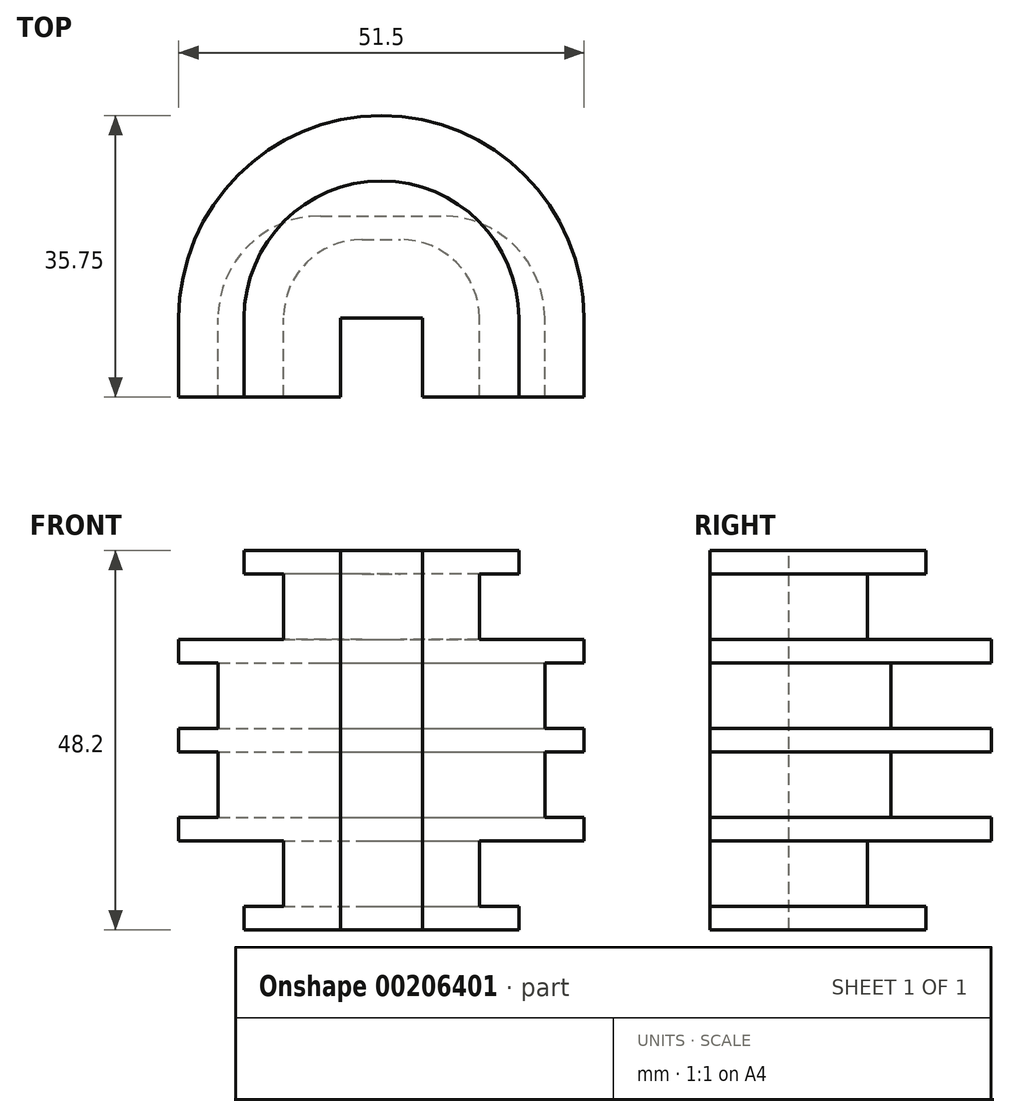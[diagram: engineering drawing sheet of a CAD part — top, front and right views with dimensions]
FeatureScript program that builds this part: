
annotation { "Feature Type Name" : "Feature", "Feature Type Description" : "" }
export const myFeature = defineFeature(function(context is Context, id is Id, definition is map)
    precondition{}
    {
        {
            assignVariable(context, id + "F0", {"name" : "slot", "anyValue" : 8.3});
        }
        {
            var Q0;
            Q0=qCreatedBy(makeId("Top.planeOp"),FACE);
            var sketch = newSketch(context, id + "F1", { "sketchPlane" : qUnion([Q0])});
            skLineSegment(sketch, "E0", {"start": v(-12.45, 0) * mm, "end": v(12.45, 0) * mm});
            skLineSegment(sketch, "E1", {"start": v(0, 10) * mm, "end": v(2.45, 10) * mm});
            skArc(sketch, "E2", {"start": v(2.45, 10) * mm, "mid": v(9.52, 7.07) * mm, "end": v(12.45, 0) * mm});
            skLineSegment(sketch, "E3.MirrorCS", {"start": v(0, 10) * mm, "end": v(-2.45, 10) * mm});
            skArc(sketch, "E4.MirrorCS", {"start": v(-2.45, 10) * mm, "mid": v(-9.52, 7.07) * mm, "end": v(-12.45, 0) * mm});
            skSolve(sketch);
        }
        {
            var Q0;
            Q0 = qSketchRegion(id + "F1", true);
            extrude(context, id + "F2", {"entities" : qUnion([Q0]), "depth" : (getVariable(context, 'slot')) * mm});
        }
        {
            var Q0;
            Q0=makeQuery(id+"F2.opExtrude","CAP_FACE",FACE,{"disambiguationData":[OSD([sQuery(id+"F1.wireOp",EDGE,"E0"),sQuery(id+"F1.wireOp",EDGE,"l2TL0GOp-FfTA-6rHu-1I54-9TwRSkG5pjle")])],"isStart":false});
            var sketch = newSketch(context, id + "F3", { "sketchPlane" : qUnion([Q0])});
            skArc(sketch, "E5", {"start": v(-17.45, 0) * mm, "mid": v(0, 17.45) * mm, "end": v(17.45, 0) * mm});
            skLineSegment(sketch, "E6", {"start": v(-17.45, 0) * mm, "end": v(17.45, 0) * mm});
            skSolve(sketch);
        }
        {
            var Q0;
            Q0 = qSketchRegion(id + "F3", true);
            extrude(context, id + "F4", {"entities" : qUnion([Q0]), "operationType" : NewBodyOperationType.ADD, "depth" : 3 * mm});
        }
        {
            var Q0;
            Q0=makeQuery(id+"F2.opExtrude","CAP_FACE",FACE,{"disambiguationData":[OSD([sQuery(id+"F1.wireOp",EDGE,"E0"),sQuery(id+"F1.wireOp",EDGE,"l2TL0GOp-FfTA-6rHu-1I54-9TwRSkG5pjle")])],"isStart":true});
            var sketch = newSketch(context, id + "F5", { "sketchPlane" : qUnion([Q0])});
            skArc(sketch, "E7", {"start": v(25.75, 0) * mm, "mid": v(0, -25.75) * mm, "end": v(-25.75, 0) * mm});
            skLineSegment(sketch, "E8", {"start": v(25.75, 0) * mm, "end": v(-25.75, 0) * mm});
            skSolve(sketch);
        }
        {
            var Q0;
            Q0 = qSketchRegion(id + "F5", true);
            extrude(context, id + "F6", {"entities" : qUnion([Q0]), "operationType" : NewBodyOperationType.ADD, "depth" : 3 * mm});
        }
        {
            var Q0;
            Q0=makeQuery(id+"F6.opExtrude","CAP_FACE",FACE,{"disambiguationData":[OSD([sQuery(id+"F5.wireOp",EDGE,"E7"),sQuery(id+"F5.wireOp",EDGE,"E8")])],"isStart":false});
            var sketch = newSketch(context, id + "F7", { "sketchPlane" : qUnion([Q0])});
            skLineSegment(sketch, "E9", {"start": v(20.75, 0) * mm, "end": v(-20.75, 0) * mm});
            skLineSegment(sketch, "E10", {"start": v(-7.75, -13) * mm, "end": v(0, -13) * mm});
            skArc(sketch, "E11", {"start": v(-7.75, -13) * mm, "mid": v(-16.94, -9.2) * mm, "end": v(-20.75, 0) * mm});
            skLineSegment(sketch, "E12.MirrorCS", {"start": v(7.75, -13) * mm, "end": v(0, -13) * mm});
            skArc(sketch, "E13.MirrorCS", {"start": v(7.75, -13) * mm, "mid": v(16.94, -9.2) * mm, "end": v(20.75, 0) * mm});
            skSolve(sketch);
        }
        {
            var Q0;
            Q0 = qSketchRegion(id + "F7", true);
            extrude(context, id + "F8", {"entities" : qUnion([Q0]), "operationType" : NewBodyOperationType.ADD, "depth" : (getVariable(context, 'slot')) * mm});
        }
        {
            var Q0;
            Q0=makeQuery(id+"F8.opExtrude","CAP_FACE",FACE,{"disambiguationData":[OSD([sQuery(id+"F7.wireOp",EDGE,"E9"),sQuery(id+"F7.wireOp",EDGE,"E10"),sQuery(id+"F7.wireOp",EDGE,"E11"),sQuery(id+"F7.wireOp",EDGE,"E12.MirrorCS"),sQuery(id+"F7.wireOp",EDGE,"E13.MirrorCS")])],"isStart":false});
            var sketch = newSketch(context, id + "F9", { "sketchPlane" : qUnion([Q0])});
            skArc(sketch, "E14", {"start": v(25.75, 0) * mm, "mid": v(0, -25.75) * mm, "end": v(-25.75, 0) * mm});
            skPoint(sketch, "E14.startSnap0", {"position": v(0, 0) * mm});
            skLineSegment(sketch, "E15", {"start": v(25.75, 0) * mm, "end": v(-25.75, 0) * mm});
            skSolve(sketch);
        }
        {
            var Q0;
            Q0 = qSketchRegion(id + "F9", true);
            extrude(context, id + "F10", {"entities" : qUnion([Q0]), "operationType" : NewBodyOperationType.ADD, "depth" : 3 * mm});
        }
        {
            var Q0;
            Q0=makeQuery(id+"F10.opExtrude","CAP_FACE",FACE,{"disambiguationData":[OSD([sQuery(id+"F9.wireOp",EDGE,"E14"),sQuery(id+"F9.wireOp",EDGE,"E15")])],"isStart":false});
            var sketch = newSketch(context, id + "F11", { "sketchPlane" : qUnion([Q0])});
            skLineSegment(sketch, "E16", {"start": v(20.75, 0) * mm, "end": v(-20.75, 0) * mm});
            skLineSegment(sketch, "E17", {"start": v(-7.75, -13) * mm, "end": v(0, -13) * mm});
            skArc(sketch, "E18", {"start": v(-7.75, -13) * mm, "mid": v(-16.94, -9.2) * mm, "end": v(-20.75, 0) * mm});
            skLineSegment(sketch, "E19.MirrorCS", {"start": v(7.75, -13) * mm, "end": v(0, -13) * mm});
            skArc(sketch, "E20.MirrorCS", {"start": v(7.75, -13) * mm, "mid": v(16.94, -9.2) * mm, "end": v(20.75, 0) * mm});
            skSolve(sketch);
        }
        {
            var Q0;
            Q0 = qSketchRegion(id + "F11", true);
            extrude(context, id + "F12", {"entities" : qUnion([Q0]), "operationType" : NewBodyOperationType.ADD, "depth" : (getVariable(context, 'slot')) * mm});
        }
        {
            var Q0;
            Q0=makeQuery(id+"F12.opExtrude","CAP_FACE",FACE,{"disambiguationData":[OSD([sQuery(id+"F11.wireOp",EDGE,"E16"),sQuery(id+"F11.wireOp",EDGE,"E17"),sQuery(id+"F11.wireOp",EDGE,"E18"),sQuery(id+"F11.wireOp",EDGE,"E19.MirrorCS"),sQuery(id+"F11.wireOp",EDGE,"E20.MirrorCS")])],"isStart":false});
            var sketch = newSketch(context, id + "F13", { "sketchPlane" : qUnion([Q0])});
            skArc(sketch, "E21", {"start": v(25.75, 0) * mm, "mid": v(0, -25.75) * mm, "end": v(-25.75, 0) * mm});
            skPoint(sketch, "E21.startSnap0", {"position": v(0, 0) * mm});
            skLineSegment(sketch, "E22", {"start": v(25.75, 0) * mm, "end": v(-25.75, 0) * mm});
            skSolve(sketch);
        }
        {
            var Q0;
            Q0 = qSketchRegion(id + "F13", true);
            extrude(context, id + "F14", {"entities" : qUnion([Q0]), "operationType" : NewBodyOperationType.ADD, "depth" : 3 * mm});
        }
        {
            var Q0;
            Q0=makeQuery(id+"F14.opExtrude","CAP_FACE",FACE,{"disambiguationData":[OSD([sQuery(id+"F13.wireOp",EDGE,"E21"),sQuery(id+"F13.wireOp",EDGE,"E22")])],"isStart":false});
            var sketch = newSketch(context, id + "F15", { "sketchPlane" : qUnion([Q0])});
            skLineSegment(sketch, "E23", {"start": v(0, -10) * mm, "end": v(2.45, -10) * mm});
            skArc(sketch, "E24", {"start": v(2.45, -10) * mm, "mid": v(9.52, -7.07) * mm, "end": v(12.45, 0) * mm});
            skLineSegment(sketch, "E25", {"start": v(12.45, 0) * mm, "end": v(0, 0) * mm});
            skLineSegment(sketch, "E26.MirrorCS", {"start": v(0, -10) * mm, "end": v(-2.45, -10) * mm});
            skArc(sketch, "E27.MirrorCS", {"start": v(-2.45, -10) * mm, "mid": v(-9.52, -7.07) * mm, "end": v(-12.45, 0) * mm});
            skLineSegment(sketch, "E28.MirrorCS", {"start": v(-12.45, 0) * mm, "end": v(0, 0) * mm});
            skSolve(sketch);
        }
        {
            var Q0;
            Q0 = qSketchRegion(id + "F15", true);
            extrude(context, id + "F16", {"entities" : qUnion([Q0]), "operationType" : NewBodyOperationType.ADD, "depth" : (getVariable(context, 'slot')) * mm});
        }
        {
            var Q0;
            Q0=makeQuery(id+"F16.opExtrude","CAP_FACE",FACE,{"disambiguationData":[OSD([sQuery(id+"F15.wireOp",EDGE,"E23"),sQuery(id+"F15.wireOp",EDGE,"E24"),sQuery(id+"F15.wireOp",EDGE,"E25"),sQuery(id+"F15.wireOp",EDGE,"E26.MirrorCS"),sQuery(id+"F15.wireOp",EDGE,"E27.MirrorCS"),sQuery(id+"F15.wireOp",EDGE,"E28.MirrorCS")])],"isStart":false});
            var sketch = newSketch(context, id + "F17", { "sketchPlane" : qUnion([Q0])});
            skArc(sketch, "E29", {"start": v(17.45, 0) * mm, "mid": v(0, -17.45) * mm, "end": v(-17.45, 0) * mm});
            skPoint(sketch, "E29.startSnap0", {"position": v(0, 0) * mm});
            skLineSegment(sketch, "E30", {"start": v(17.45, 0) * mm, "end": v(-17.45, 0) * mm});
            skSolve(sketch);
        }
        {
            var Q0;
            Q0 = qSketchRegion(id + "F17", true);
            extrude(context, id + "F18", {"entities" : qUnion([Q0]), "operationType" : NewBodyOperationType.ADD, "depth" : 3 * mm});
        }
        {
            var Q0;
            Q0=makeQuery(id+"F18.boolean.opBoolean","MERGE",FACE,{"derivedFrom":[makeQuery(id+"F16.boolean.opBoolean","MERGE",FACE,{"derivedFrom":[makeQuery(id+"F14.boolean.opBoolean","MERGE",FACE,{"derivedFrom":[makeQuery(id+"F12.boolean.opBoolean","MERGE",FACE,{"derivedFrom":[makeQuery(id+"F10.boolean.opBoolean","MERGE",FACE,{"derivedFrom":[makeQuery(id+"F8.boolean.opBoolean","MERGE",FACE,{"derivedFrom":[makeQuery(id+"F6.boolean.opBoolean","MERGE",FACE,{"derivedFrom":[makeQuery(id+"F4.boolean.opBoolean","MERGE",FACE,{"derivedFrom":[makeQuery(id+"F2.opExtrude","SWEPT_FACE",FACE,{"disambiguationData":[OSD([sQuery(id+"F1.wireOp",EDGE,"E0")])]}),makeQuery(id+"F4.opExtrude","SWEPT_FACE",FACE,{"disambiguationData":[OSD([sQuery(id+"F3.wireOp",EDGE,"E6")])]})]}),makeQuery(id+"F6.opExtrude","SWEPT_FACE",FACE,{"disambiguationData":[OSD([sQuery(id+"F5.wireOp",EDGE,"E8")])]})]}),makeQuery(id+"F8.opExtrude","SWEPT_FACE",FACE,{"disambiguationData":[OSD([sQuery(id+"F7.wireOp",EDGE,"E9")])]})]}),makeQuery(id+"F10.opExtrude","SWEPT_FACE",FACE,{"disambiguationData":[OSD([sQuery(id+"F9.wireOp",EDGE,"E15")])]})]}),makeQuery(id+"F12.opExtrude","SWEPT_FACE",FACE,{"disambiguationData":[OSD([sQuery(id+"F11.wireOp",EDGE,"E16")])]})]}),makeQuery(id+"F14.opExtrude","SWEPT_FACE",FACE,{"disambiguationData":[OSD([sQuery(id+"F13.wireOp",EDGE,"E22")])]})]}),makeQuery(id+"F16.opExtrude","SWEPT_FACE",FACE,{"disambiguationData":[OSD([sQuery(id+"F15.wireOp",EDGE,"E25"),sQuery(id+"F15.wireOp",EDGE,"E28.MirrorCS")])]})]}),makeQuery(id+"F18.opExtrude","SWEPT_FACE",FACE,{"disambiguationData":[OSD([sQuery(id+"F17.wireOp",EDGE,"E30")])]})]});
            var sketch = newSketch(context, id + "F19", { "sketchPlane" : qUnion([Q0])});
            skLineSegment(sketch, "E31", {"start": v(17.45, -36.9) * mm, "end": v(17.45, -33.9) * mm});
            skLineSegment(sketch, "E32", {"start": v(17.45, -33.9) * mm, "end": v(12.45, -33.9) * mm});
            skLineSegment(sketch, "E33", {"start": v(12.45, -33.9) * mm, "end": v(12.45, -25.6) * mm});
            skLineSegment(sketch, "E34", {"start": v(12.45, -25.6) * mm, "end": v(25.75, -25.6) * mm});
            skLineSegment(sketch, "E35", {"start": v(25.75, -25.6) * mm, "end": v(25.75, -22.6) * mm});
            skLineSegment(sketch, "E36", {"start": v(25.75, -22.6) * mm, "end": v(20.75, -22.6) * mm});
            skLineSegment(sketch, "E37", {"start": v(20.75, -22.6) * mm, "end": v(20.75, -14.3) * mm});
            skLineSegment(sketch, "E38", {"start": v(20.75, -14.3) * mm, "end": v(25.75, -14.3) * mm});
            skLineSegment(sketch, "E39", {"start": v(25.75, -14.3) * mm, "end": v(25.75, -11.3) * mm});
            skLineSegment(sketch, "E40", {"start": v(25.75, -11.3) * mm, "end": v(20.75, -11.3) * mm});
            skLineSegment(sketch, "E41", {"start": v(20.75, -11.3) * mm, "end": v(20.75, -3) * mm});
            skLineSegment(sketch, "E42", {"start": v(20.75, -3) * mm, "end": v(25.75, -3) * mm});
            skLineSegment(sketch, "E43", {"start": v(25.75, -3) * mm, "end": v(25.75, 0) * mm});
            skLineSegment(sketch, "E44", {"start": v(25.75, 0) * mm, "end": v(12.45, 0) * mm});
            skLineSegment(sketch, "E45", {"start": v(12.45, 0) * mm, "end": v(12.45, 8.3) * mm});
            skLineSegment(sketch, "E46", {"start": v(12.45, 8.3) * mm, "end": v(17.45, 8.3) * mm});
            skLineSegment(sketch, "E47", {"start": v(17.45, 8.3) * mm, "end": v(17.45, 11.3) * mm});
            skLineSegment(sketch, "E48", {"start": v(17.45, 11.3) * mm, "end": v(0, 11.3) * mm});
            skLineSegment(sketch, "E49", {"start": v(17.45, -36.9) * mm, "end": v(0, -36.9) * mm});
            skLineSegment(sketch, "E50.MirrorCS", {"start": v(-17.45, -36.9) * mm, "end": v(0, -36.9) * mm});
            skLineSegment(sketch, "E51.MirrorCS", {"start": v(-17.45, -36.9) * mm, "end": v(-17.45, -33.9) * mm});
            skLineSegment(sketch, "E52.MirrorCS", {"start": v(-17.45, -33.9) * mm, "end": v(-12.45, -33.9) * mm});
            skLineSegment(sketch, "E53.MirrorCS", {"start": v(-12.45, -33.9) * mm, "end": v(-12.45, -25.6) * mm});
            skLineSegment(sketch, "E54.MirrorCS", {"start": v(-12.45, -25.6) * mm, "end": v(-25.75, -25.6) * mm});
            skLineSegment(sketch, "E55.MirrorCS", {"start": v(-25.75, -25.6) * mm, "end": v(-25.75, -22.6) * mm});
            skLineSegment(sketch, "E56.MirrorCS", {"start": v(-25.75, -22.6) * mm, "end": v(-20.75, -22.6) * mm});
            skLineSegment(sketch, "E57.MirrorCS", {"start": v(-20.75, -22.6) * mm, "end": v(-20.75, -14.3) * mm});
            skLineSegment(sketch, "E58.MirrorCS", {"start": v(-20.75, -14.3) * mm, "end": v(-25.75, -14.3) * mm});
            skLineSegment(sketch, "E59.MirrorCS", {"start": v(-25.75, -14.3) * mm, "end": v(-25.75, -11.3) * mm});
            skLineSegment(sketch, "E60.MirrorCS", {"start": v(-25.75, -11.3) * mm, "end": v(-20.75, -11.3) * mm});
            skLineSegment(sketch, "E61.MirrorCS", {"start": v(-20.75, -11.3) * mm, "end": v(-20.75, -3) * mm});
            skLineSegment(sketch, "E62.MirrorCS", {"start": v(-20.75, -3) * mm, "end": v(-25.75, -3) * mm});
            skLineSegment(sketch, "E63.MirrorCS", {"start": v(-25.75, -3) * mm, "end": v(-25.75, 0) * mm});
            skLineSegment(sketch, "E64.MirrorCS", {"start": v(-25.75, 0) * mm, "end": v(-12.45, 0) * mm});
            skLineSegment(sketch, "E65.MirrorCS", {"start": v(-12.45, 0) * mm, "end": v(-12.45, 8.3) * mm});
            skLineSegment(sketch, "E66.MirrorCS", {"start": v(-12.45, 8.3) * mm, "end": v(-17.45, 8.3) * mm});
            skLineSegment(sketch, "E67.MirrorCS", {"start": v(-17.45, 8.3) * mm, "end": v(-17.45, 11.3) * mm});
            skLineSegment(sketch, "E68.MirrorCS", {"start": v(-17.45, 11.3) * mm, "end": v(0, 11.3) * mm});
            skSolve(sketch);
        }
        {
            var Q0;
            Q0 = qSketchRegion(id + "F19", true);
            extrude(context, id + "F20", {"entities" : qUnion([Q0]), "operationType" : NewBodyOperationType.ADD, "depth" : 10 * mm});
        }
        {
            var Q0;
            Q0=makeQuery(id+"F20.opExtrude","CAP_FACE",FACE,{"disambiguationData":[OSD([sQuery(id+"F19.wireOp",EDGE,"E31"),sQuery(id+"F19.wireOp",EDGE,"E32"),sQuery(id+"F19.wireOp",EDGE,"E33"),sQuery(id+"F19.wireOp",EDGE,"E34"),sQuery(id+"F19.wireOp",EDGE,"E35"),sQuery(id+"F19.wireOp",EDGE,"E36"),sQuery(id+"F19.wireOp",EDGE,"E37"),sQuery(id+"F19.wireOp",EDGE,"E38"),sQuery(id+"F19.wireOp",EDGE,"E39"),sQuery(id+"F19.wireOp",EDGE,"E40"),sQuery(id+"F19.wireOp",EDGE,"E41"),sQuery(id+"F19.wireOp",EDGE,"E42"),sQuery(id+"F19.wireOp",EDGE,"E43"),sQuery(id+"F19.wireOp",EDGE,"E44"),sQuery(id+"F19.wireOp",EDGE,"E45"),sQuery(id+"F19.wireOp",EDGE,"E46"),sQuery(id+"F19.wireOp",EDGE,"E47"),sQuery(id+"F19.wireOp",EDGE,"E48"),sQuery(id+"F19.wireOp",EDGE,"E49"),sQuery(id+"F19.wireOp",EDGE,"E50.MirrorCS"),sQuery(id+"F19.wireOp",EDGE,"E51.MirrorCS"),sQuery(id+"F19.wireOp",EDGE,"E52.MirrorCS"),sQuery(id+"F19.wireOp",EDGE,"E53.MirrorCS"),sQuery(id+"F19.wireOp",EDGE,"E54.MirrorCS"),sQuery(id+"F19.wireOp",EDGE,"E55.MirrorCS"),sQuery(id+"F19.wireOp",EDGE,"E56.MirrorCS"),sQuery(id+"F19.wireOp",EDGE,"E57.MirrorCS"),sQuery(id+"F19.wireOp",EDGE,"E58.MirrorCS"),sQuery(id+"F19.wireOp",EDGE,"E59.MirrorCS"),sQuery(id+"F19.wireOp",EDGE,"E60.MirrorCS"),sQuery(id+"F19.wireOp",EDGE,"E61.MirrorCS"),sQuery(id+"F19.wireOp",EDGE,"E62.MirrorCS"),sQuery(id+"F19.wireOp",EDGE,"E63.MirrorCS"),sQuery(id+"F19.wireOp",EDGE,"E64.MirrorCS"),sQuery(id+"F19.wireOp",EDGE,"E65.MirrorCS"),sQuery(id+"F19.wireOp",EDGE,"E66.MirrorCS"),sQuery(id+"F19.wireOp",EDGE,"E67.MirrorCS"),sQuery(id+"F19.wireOp",EDGE,"E68.MirrorCS")])],"isStart":false});
            var sketch = newSketch(context, id + "F21", { "sketchPlane" : qUnion([Q0])});
            skLineSegment(sketch, "E69", {"start": v(0, -36.9) * mm, "end": v(5.2, -36.9) * mm});
            skLineSegment(sketch, "E70", {"start": v(5.2, -36.9) * mm, "end": v(5.2, 11.3) * mm});
            skLineSegment(sketch, "E71", {"start": v(5.2, 11.3) * mm, "end": v(0, 11.3) * mm});
            skLineSegment(sketch, "E72.MirrorCS", {"start": v(0, -36.9) * mm, "end": v(-5.2, -36.9) * mm});
            skLineSegment(sketch, "E73.MirrorCS", {"start": v(-5.2, -36.9) * mm, "end": v(-5.2, 11.3) * mm});
            skLineSegment(sketch, "E74.MirrorCS", {"start": v(-5.2, 11.3) * mm, "end": v(0, 11.3) * mm});
            skSolve(sketch);
        }
        {
            var Q0;
            Q0 = qSketchRegion(id + "F21", true);
            extrude(context, id + "F22", {"entities" : qUnion([Q0]), "operationType" : NewBodyOperationType.REMOVE, "oppositeDirection" : true, "depth" : 10 * mm});
        }
    });
